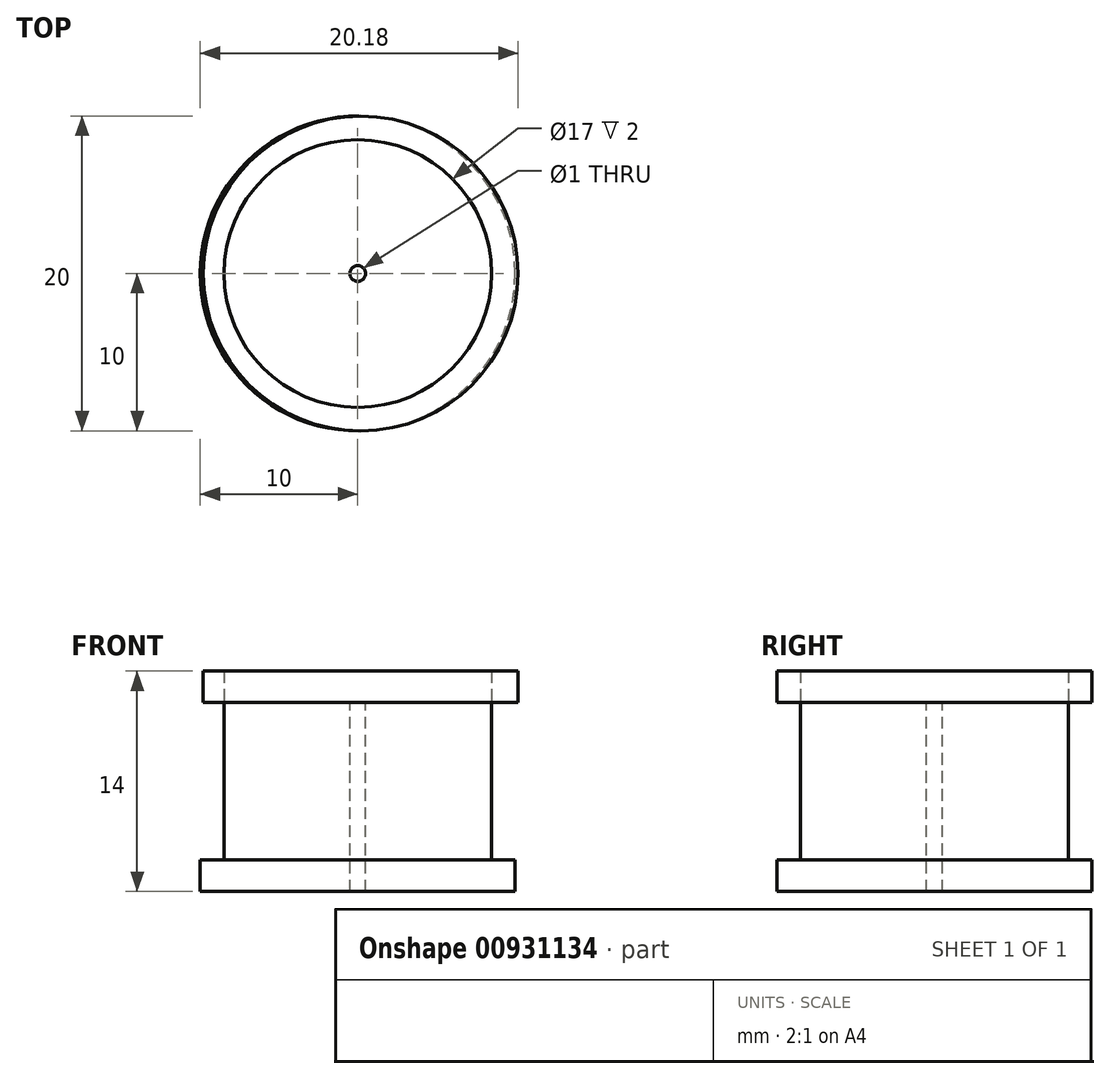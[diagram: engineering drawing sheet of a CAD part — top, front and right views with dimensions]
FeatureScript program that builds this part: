
annotation { "Feature Type Name" : "Feature", "Feature Type Description" : "" }
export const myFeature = defineFeature(function(context is Context, id is Id, definition is map)
    precondition{}
    {
        {
            var Q0;
            Q0=qCreatedBy(makeId("Top.planeOp"),FACE);
            var sketch = newSketch(context, id + "F0", { "sketchPlane" : qUnion([Q0])});
            skCircle(sketch, "E0", {"center": v(0, 0) * mm, "radius": 10 * mm});
            skCircle(sketch, "E1", {"center": v(0, 0) * mm, "radius": 0.5 * mm});
            skSolve(sketch);
        }
        {
            var Q0;
            Q0=makeQuery(id+"F0.imprint","IMPRINT",FACE,{"disambiguationData":[TD([[makeQuery(id+"F0.imprint","IMPRINT",EDGE,{"derivedFrom":sQuery(id+"F0.wireOp",EDGE,"E0")}),1.0]])]});
            extrude(context, id + "F1", {"entities" : qUnion([Q0]), "oppositeDirection" : true, "depth" : 2 * mm, "offsetDistance" : 25 * mm});
        }
        {
            var Q0;
            Q0=makeQuery(id+"F1.opExtrude","CAP_FACE",FACE,{"disambiguationData":[OSD([sQuery(id+"F0.wireOp",EDGE,"E0"),sQuery(id+"F0.wireOp",EDGE,"E1")])],"isStart":true});
            var sketch = newSketch(context, id + "F2", { "sketchPlane" : qUnion([Q0])});
            skCircle(sketch, "E2", {"center": v(0, 0) * mm, "radius": 8.5 * mm});
            skCircle(sketch, "E3", {"center": v(0, 0) * mm, "radius": 0.5 * mm});
            skSolve(sketch);
        }
        {
            var Q0;
            Q0=makeQuery(id+"F2.imprint","IMPRINT",FACE,{"disambiguationData":[TD([[makeQuery(id+"F2.imprint","IMPRINT",EDGE,{"derivedFrom":sQuery(id+"F2.wireOp",EDGE,"E2")}),1.0]])]});
            extrude(context, id + "F3", {"entities" : qUnion([Q0]), "operationType" : NewBodyOperationType.ADD, "depth" : 10 * mm, "offsetDistance" : 25 * mm});
        }
        {
            var Q0;
            Q0=makeQuery(id+"F3.opExtrude","CAP_FACE",FACE,{"disambiguationData":[OSD([sQuery(id+"F2.wireOp",EDGE,"E2"),sQuery(id+"F2.wireOp",EDGE,"E3")])],"isStart":false});
            var sketch = newSketch(context, id + "F4", { "sketchPlane" : qUnion([Q0])});
            skCircle(sketch, "E4", {"center": v(0, 0) * mm, "radius": 0.5 * mm});
            skCircle(sketch, "E5", {"center": v(0.18, 0) * mm, "radius": 10 * mm});
            skSolve(sketch);
        }
        {
            var Q0;
            Q0=makeQuery(id+"F4.imprint","IMPRINT",FACE,{"disambiguationData":[TD([[makeQuery(id+"F4.imprint","IMPRINT",EDGE,{"derivedFrom":sQuery(id+"F4.wireOp",EDGE,"E5")}),1.0]])]});
            extrude(context, id + "F5", {"entities" : qUnion([Q0]), "depth" : 2 * mm, "offsetDistance" : 25 * mm});
        }
    });
